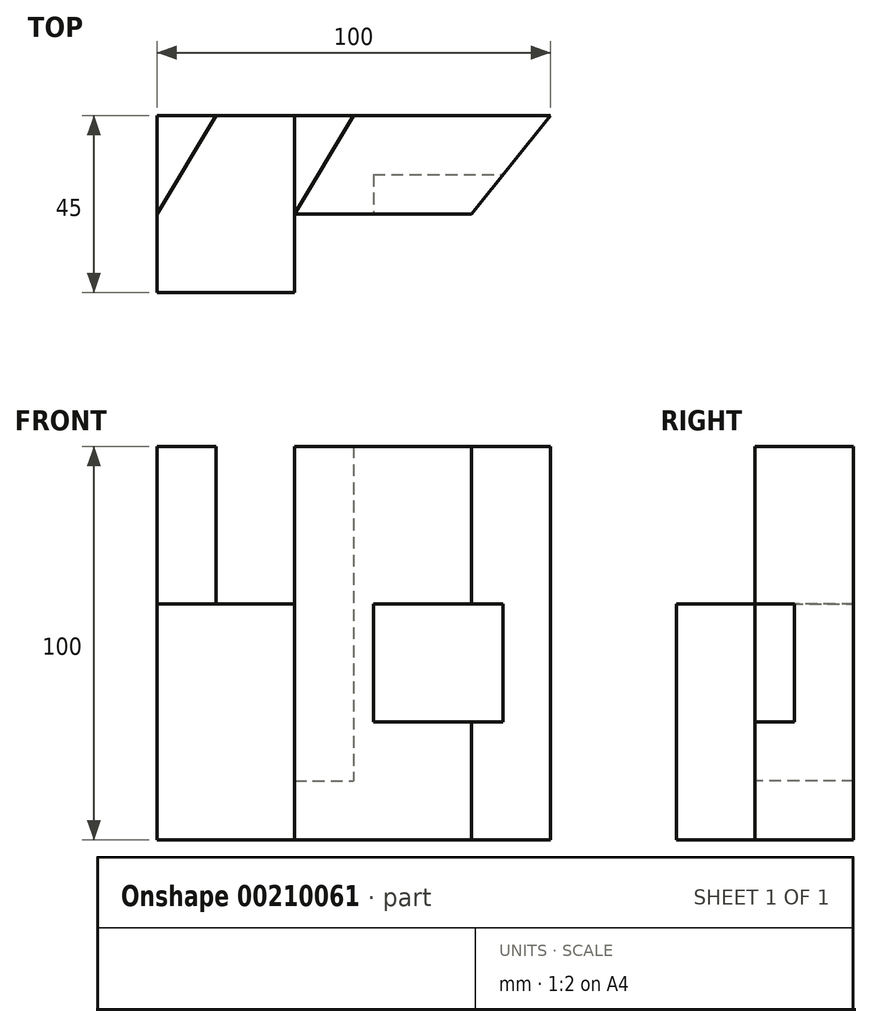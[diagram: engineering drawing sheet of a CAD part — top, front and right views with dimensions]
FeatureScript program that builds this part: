
annotation { "Feature Type Name" : "Feature", "Feature Type Description" : "" }
export const myFeature = defineFeature(function(context is Context, id is Id, definition is map)
    precondition{}
    {
        {
            var Q0;
            Q0=qCreatedBy(makeId("Top.planeOp"),FACE);
            var sketch = newSketch(context, id + "F0", { "sketchPlane" : qUnion([Q0])});
            skLineSegment(sketch, "E0.bottom", {"start": v(0, 0) * mm, "end": v(-35, 0) * mm});
            skLineSegment(sketch, "E0.top", {"start": v(0, -45) * mm, "end": v(-35, -45) * mm});
            skLineSegment(sketch, "E0.left", {"start": v(0, 0) * mm, "end": v(0, -45) * mm});
            skLineSegment(sketch, "E0.right", {"start": v(-35, 0) * mm, "end": v(-35, -45) * mm});
            skSolve(sketch);
        }
        {
            var Q0;
            Q0 = qSketchRegion(id + "F0", true);
            extrude(context, id + "F1", {"entities" : qUnion([Q0]), "depth" : 60 * mm});
        }
        {
            var Q0;
            Q0=makeQuery(id+"F1.opExtrude","CAP_FACE",FACE,{"disambiguationData":[OSD([sQuery(id+"F0.wireOp",EDGE,"E0.bottom"),sQuery(id+"F0.wireOp",EDGE,"E0.top"),sQuery(id+"F0.wireOp",EDGE,"E0.left"),sQuery(id+"F0.wireOp",EDGE,"E0.right")])],"isStart":false});
            var sketch = newSketch(context, id + "F2", { "sketchPlane" : qUnion([Q0])});
            skLineSegment(sketch, "E1", {"start": v(-20, 0) * mm, "end": v(-35, 0) * mm});
            skLineSegment(sketch, "E2", {"start": v(-35, 0) * mm, "end": v(-35, -25) * mm});
            skLineSegment(sketch, "E3", {"start": v(-35, -25) * mm, "end": v(-20, 0) * mm});
            skSolve(sketch);
        }
        {
            var Q0;
            Q0 = qSketchRegion(id + "F2", true);
            extrude(context, id + "F3", {"entities" : qUnion([Q0]), "operationType" : NewBodyOperationType.ADD, "depth" : 40 * mm});
        }
        {
            var Q0;
            Q0=qCreatedBy(makeId("Top.planeOp"),FACE);
            var sketch = newSketch(context, id + "F4", { "sketchPlane" : qUnion([Q0])});
            skLineSegment(sketch, "E4", {"start": v(0, 0) * mm, "end": v(0, -25) * mm});
            skLineSegment(sketch, "E5", {"start": v(0, -25) * mm, "end": v(45, -25) * mm});
            skLineSegment(sketch, "E6", {"start": v(45, -25) * mm, "end": v(65, 0) * mm});
            skLineSegment(sketch, "E7", {"start": v(65, 0) * mm, "end": v(0, 0) * mm});
            skSolve(sketch);
        }
        {
            var Q0;
            Q0 = qSketchRegion(id + "F4", true);
            extrude(context, id + "F5", {"entities" : qUnion([Q0]), "operationType" : NewBodyOperationType.ADD, "depth" : 15 * mm});
        }
        {
            var Q0;
            Q0=makeQuery(id+"F5.boolean.opBoolean","MERGE",FACE,{"derivedFrom":[makeQuery(id+"F1.opExtrude","CAP_FACE",FACE,{"disambiguationData":[OSD([sQuery(id+"F0.wireOp",EDGE,"E0.bottom"),sQuery(id+"F0.wireOp",EDGE,"E0.top"),sQuery(id+"F0.wireOp",EDGE,"E0.left"),sQuery(id+"F0.wireOp",EDGE,"E0.right")])],"isStart":true}),makeQuery(id+"F5.opExtrude","CAP_FACE",FACE,{"disambiguationData":[OSD([sQuery(id+"F4.wireOp",EDGE,"E4"),sQuery(id+"F4.wireOp",EDGE,"E5"),sQuery(id+"F4.wireOp",EDGE,"E6"),sQuery(id+"F4.wireOp",EDGE,"E7")])],"isStart":true})]});
            cPlane(context, id + "F6", {"entities" : qUnion([Q0]), "cplaneType" : CPlaneType.OFFSET, "offset" : 100 * mm, "oppositeDirection" : true, "width" : 150 * mm, "height" : 150 * mm});
        }
        {
            var Q0;
            Q0=makeQuery(id+"F5.opExtrude","CAP_FACE",FACE,{"disambiguationData":[OSD([sQuery(id+"F4.wireOp",EDGE,"E4"),sQuery(id+"F4.wireOp",EDGE,"E5"),sQuery(id+"F4.wireOp",EDGE,"E6"),sQuery(id+"F4.wireOp",EDGE,"E7")])],"isStart":false});
            var sketch = newSketch(context, id + "F7", { "sketchPlane" : qUnion([Q0])});
            skLineSegment(sketch, "E8", {"start": v(65, 0) * mm, "end": v(45, -25) * mm});
            skLineSegment(sketch, "E9", {"start": v(45, -25) * mm, "end": v(0, -25) * mm});
            skLineSegment(sketch, "E10", {"start": v(0, -25) * mm, "end": v(0, -25) * mm});
            skLineSegment(sketch, "E11", {"start": v(0, -25) * mm, "end": v(15, 0) * mm});
            skLineSegment(sketch, "E12", {"start": v(15, 0) * mm, "end": v(65, 0) * mm});
            skSolve(sketch);
        }
        {
            var Q0;
            Q0 = qSketchRegion(id + "F7", true);
            var Q1;
            Q1=qCreatedBy(id+"F6.planeOp",FACE);
            extrude(context, id + "F8", {"entities" : qUnion([Q0]), "operationType" : NewBodyOperationType.ADD, "endBound" : BoundingType.UP_TO_SURFACE, "endBoundEntityFace" : qUnion([Q1]), "depth" : 85 * mm});
        }
        {
            var Q0;
            Q0=makeQuery(id+"F8.boolean.opBoolean","MERGE",FACE,{"derivedFrom":[makeQuery(id+"F5.opExtrude","SWEPT_FACE",FACE,{"disambiguationData":[OSD([sQuery(id+"F4.wireOp",EDGE,"E5")])]}),makeQuery(id+"F8.opExtrude","SWEPT_FACE",FACE,{"disambiguationData":[OSD([sQuery(id+"F7.wireOp",EDGE,"E9")])]})]});
            var sketch = newSketch(context, id + "F9", { "sketchPlane" : qUnion([Q0])});
            skLineSegment(sketch, "E13.bottom", {"start": v(20, 30) * mm, "end": v(65, 30) * mm});
            skLineSegment(sketch, "E13.top", {"start": v(20, 60) * mm, "end": v(65, 60) * mm});
            skLineSegment(sketch, "E13.left", {"start": v(20, 30) * mm, "end": v(20, 60) * mm});
            skLineSegment(sketch, "E13.right", {"start": v(65, 30) * mm, "end": v(65, 60) * mm});
            skSolve(sketch);
        }
        {
            var Q0;
            Q0 = qSketchRegion(id + "F9", true);
            extrude(context, id + "F10", {"entities" : qUnion([Q0]), "operationType" : NewBodyOperationType.REMOVE, "oppositeDirection" : true, "depth" : 10 * mm});
        }
    });
